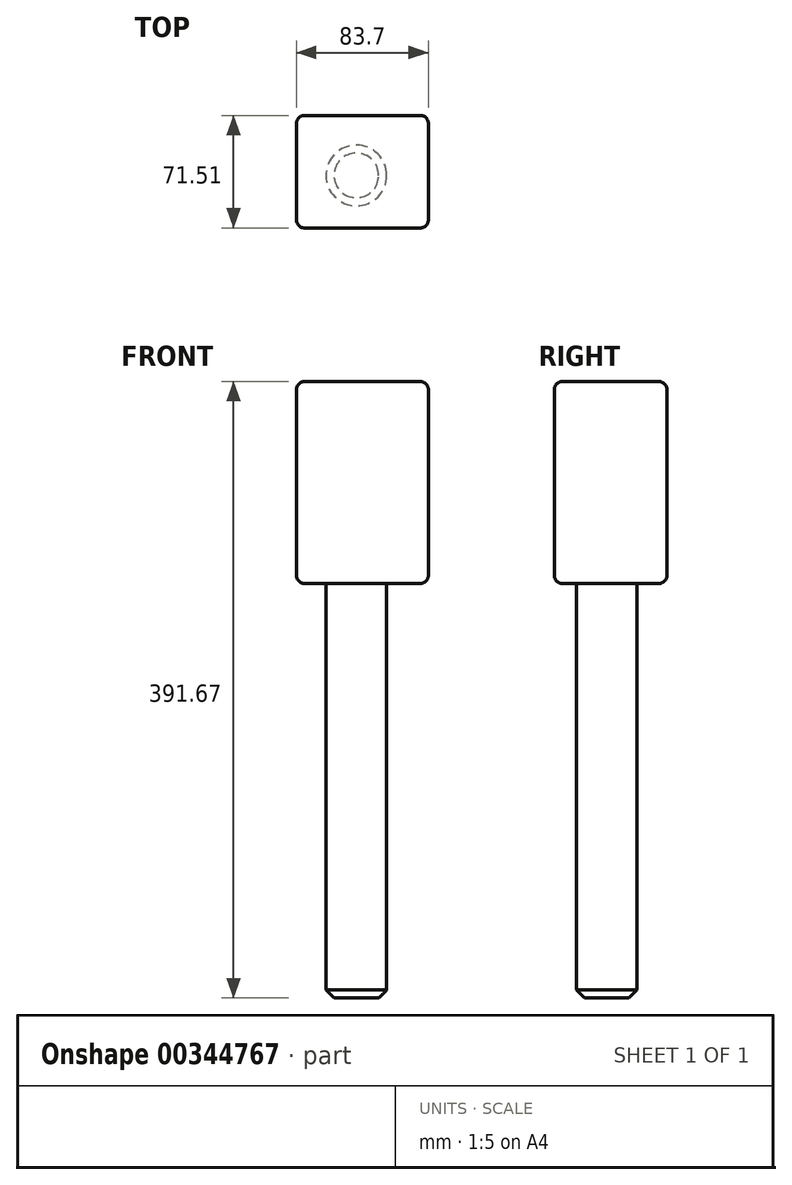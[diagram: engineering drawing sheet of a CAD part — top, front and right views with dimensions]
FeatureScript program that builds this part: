
annotation { "Feature Type Name" : "Feature", "Feature Type Description" : "" }
export const myFeature = defineFeature(function(context is Context, id is Id, definition is map)
    precondition{}
    {
        {
            var Q0;
            Q0=qCreatedBy(makeId("Top.planeOp"),FACE);
            var sketch = newSketch(context, id + "F0", { "sketchPlane" : qUnion([Q0])});
            skLineSegment(sketch, "E0.bottom", {"start": v(45.7, -33.35) * mm, "end": v(-38, -33.35) * mm});
            skLineSegment(sketch, "E0.top", {"start": v(45.7, 38.16) * mm, "end": v(-38, 38.16) * mm});
            skLineSegment(sketch, "E0.left", {"start": v(45.7, -33.35) * mm, "end": v(45.7, 38.16) * mm});
            skLineSegment(sketch, "E0.right", {"start": v(-38, -33.35) * mm, "end": v(-38, 38.16) * mm});
            skSolve(sketch);
        }
        {
            var Q0;
            Q0=makeQuery(id+"F0.imprint","IMPRINT",FACE,{"disambiguationData":[TD([[makeQuery(id+"F0.imprint","IMPRINT",EDGE,{"derivedFrom":sQuery(id+"F0.wireOp",EDGE,"E0.bottom")}),-1.0]])]});
            extrude(context, id + "F1", {"entities" : qUnion([Q0]), "depth" : 128.27 * mm});
        }
        {
            var Q0;
            Q0=makeQuery(id+"F1.opExtrude","SWEPT_FACE",FACE,{"disambiguationData":[OSD([sQuery(id+"F0.wireOp",EDGE,"E0.top")])]});
            var Q1;
            Q1=makeQuery(id+"F1.opExtrude","CAP_FACE",FACE,{"disambiguationData":[OSD([sQuery(id+"F0.wireOp",EDGE,"E0.bottom"),sQuery(id+"F0.wireOp",EDGE,"E0.top"),sQuery(id+"F0.wireOp",EDGE,"E0.left"),sQuery(id+"F0.wireOp",EDGE,"E0.right")])],"isStart":false});
            var Q2;
            Q2=makeQuery(id+"F1.opExtrude","SWEPT_FACE",FACE,{"disambiguationData":[OSD([sQuery(id+"F0.wireOp",EDGE,"E0.left")])]});
            var Q3;
            Q3=makeQuery(id+"F1.opExtrude","CAP_FACE",FACE,{"disambiguationData":[OSD([sQuery(id+"F0.wireOp",EDGE,"E0.bottom"),sQuery(id+"F0.wireOp",EDGE,"E0.top"),sQuery(id+"F0.wireOp",EDGE,"E0.left"),sQuery(id+"F0.wireOp",EDGE,"E0.right")])],"isStart":true});
            var Q4;
            Q4=makeQuery(id+"F1.opExtrude","SWEPT_FACE",FACE,{"disambiguationData":[OSD([sQuery(id+"F0.wireOp",EDGE,"E0.right")])]});
            fillet(context, id + "F2", {"entities" : qUnion([Q0, Q1, Q2, Q3, Q4]), "radius" : 5.08 * mm, "tangentPropagation" : true, "allowEdgeOverflow" : false});
        }
        {
            var Q0;
            Q0=qCreatedBy(makeId("Top.planeOp"),FACE);
            var sketch = newSketch(context, id + "F3", { "sketchPlane" : qUnion([Q0])});
            skCircle(sketch, "E1", {"center": v(0, 0) * mm, "radius": 19.26 * mm});
            skSolve(sketch);
        }
        {
            var Q0;
            Q0 = qSketchRegion(id + "F3", true);
            extrude(context, id + "F4", {"entities" : qUnion([Q0]), "operationType" : NewBodyOperationType.ADD, "oppositeDirection" : true, "depth" : 263.4 * mm});
        }
        {
            var Q0;
            Q0=makeQuery(id+"F4.opExtrude","CAP_EDGE",EDGE,{"disambiguationData":[OSD([sQuery(id+"F3.wireOp",EDGE,"E1")])],"isStart":false});
            chamfer(context, id + "F5", {"entities" : qUnion([Q0]), "width" : 5.08 * mm, "tangentPropagation" : true});
        }
    });
